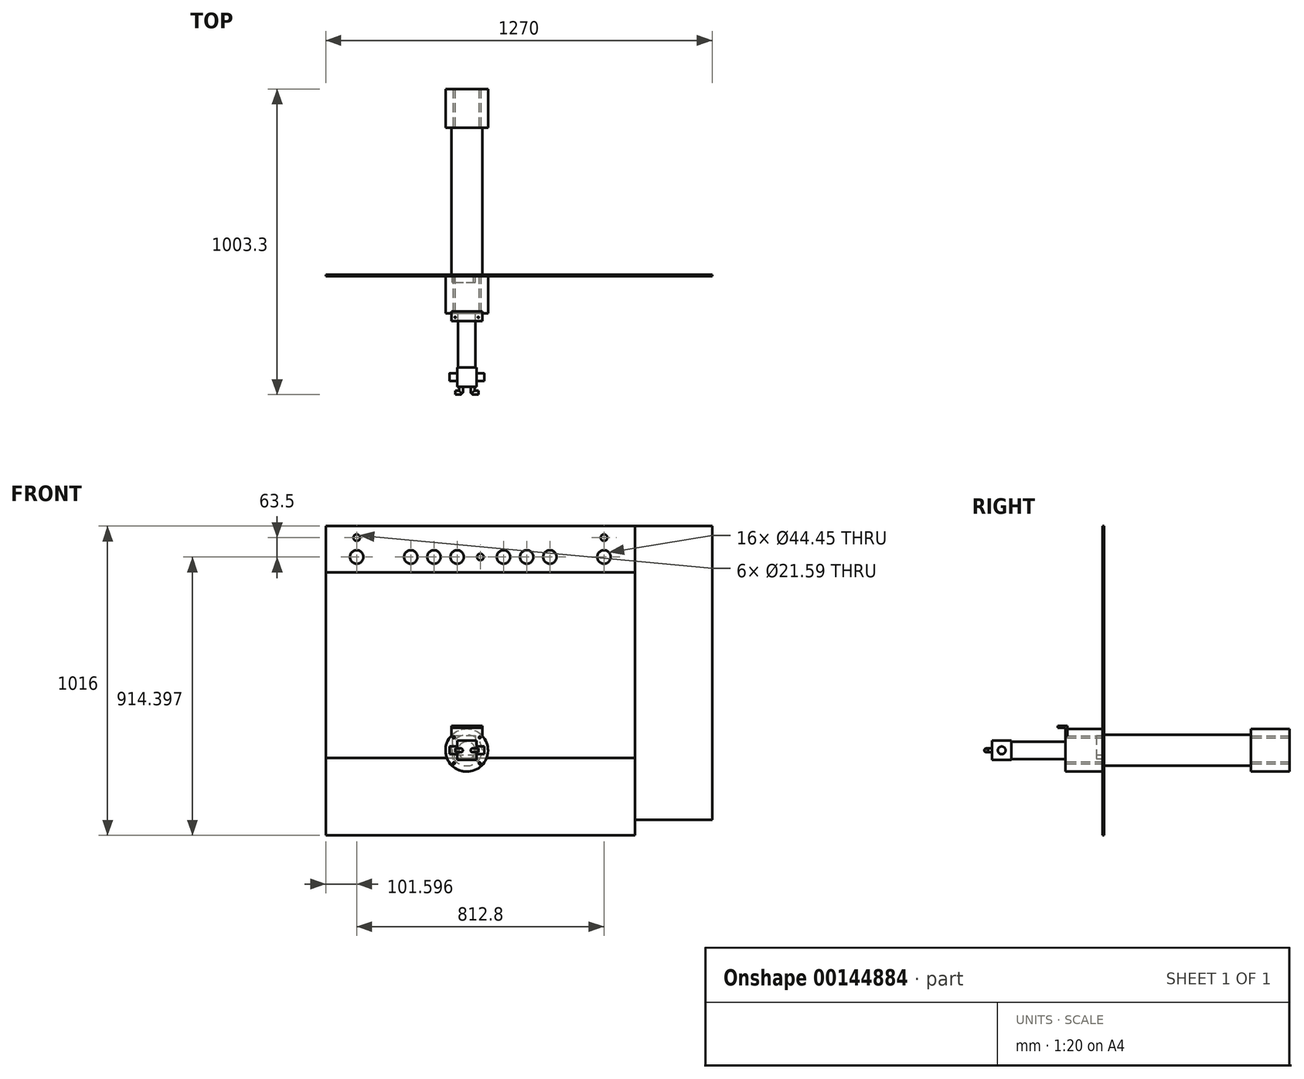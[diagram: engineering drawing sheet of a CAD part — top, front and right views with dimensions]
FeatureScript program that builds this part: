
annotation { "Feature Type Name" : "Feature", "Feature Type Description" : "" }
export const myFeature = defineFeature(function(context is Context, id is Id, definition is map)
    precondition{}
    {
        {
            var Q0;
            Q0=qCreatedBy(makeId("Front.planeOp"),FACE);
            var sketch = newSketch(context, id + "F0", { "sketchPlane" : qUnion([Q0])});
            skLineSegment(sketch, "E0.bottom", {"start": v(-463.31, 736.89) * mm, "end": v(552.69, 736.89) * mm});
            skLineSegment(sketch, "E0.top", {"start": v(-463.31, 584.49) * mm, "end": v(552.69, 584.49) * mm});
            skLineSegment(sketch, "E0.left", {"start": v(-463.31, 736.89) * mm, "end": v(-463.31, 584.49) * mm});
            skLineSegment(sketch, "E0.right", {"start": v(552.69, 736.89) * mm, "end": v(552.69, 584.49) * mm});
            skLineSegment(sketch, "E1.top", {"start": v(-463.31, -25.11) * mm, "end": v(552.69, -25.11) * mm});
            skLineSegment(sketch, "E1.left", {"start": v(-463.31, 584.49) * mm, "end": v(-463.31, -25.11) * mm});
            skLineSegment(sketch, "E1.right", {"start": v(552.69, 584.49) * mm, "end": v(552.69, -25.11) * mm});
            skLineSegment(sketch, "E2.top", {"start": v(-463.31, -279.11) * mm, "end": v(552.69, -279.11) * mm});
            skLineSegment(sketch, "E2.left", {"start": v(-463.31, -25.11) * mm, "end": v(-463.31, -279.11) * mm});
            skLineSegment(sketch, "E2.right", {"start": v(552.69, -25.11) * mm, "end": v(552.69, -279.11) * mm});
            skLineSegment(sketch, "E3.bottom", {"start": v(552.69, 736.89) * mm, "end": v(806.69, 736.89) * mm});
            skLineSegment(sketch, "E3.top", {"start": v(552.69, -228.31) * mm, "end": v(806.69, -228.31) * mm});
            skLineSegment(sketch, "E3.left", {"start": v(552.69, 736.89) * mm, "end": v(552.69, -228.31) * mm});
            skLineSegment(sketch, "E3.right", {"start": v(806.69, 736.89) * mm, "end": v(806.69, -228.31) * mm});
            skSolve(sketch);
        }
        {
            var Q0;
            Q0=makeQuery(id+"F0.imprint","IMPRINT",FACE,{"disambiguationData":[TD([[makeQuery(id+"F0.imprint","IMPRINT",EDGE,{"derivedFrom":sQuery(id+"F0.wireOp",EDGE,"E0.bottom")}),-1.0]])]});
            extrude(context, id + "F1", {"entities" : qUnion([Q0]), "depth" : 5.08 * mm});
        }
        {
            var Q0;
            Q0=makeQuery(id+"F0.imprint","IMPRINT",FACE,{"disambiguationData":[TD([[makeQuery(id+"F0.imprint","IMPRINT",EDGE,{"derivedFrom":sQuery(id+"F0.wireOp",EDGE,"E0.top")}),-1.0]])]});
            extrude(context, id + "F2", {"entities" : qUnion([Q0]), "depth" : 5.08 * mm});
        }
        {
            var Q0;
            Q0=makeQuery(id+"F0.imprint","IMPRINT",FACE,{"disambiguationData":[TD([[makeQuery(id+"F0.imprint","IMPRINT",EDGE,{"derivedFrom":sQuery(id+"F0.wireOp",EDGE,"E1.top")}),-1.0]])]});
            extrude(context, id + "F3", {"entities" : qUnion([Q0]), "depth" : 5.08 * mm});
        }
        {
            var Q0;
            {var subQ3=sQuery(id+"F0.wireOp",EDGE,"E3.bottom");Q0=makeQuery(id+"F0.imprint","IMPRINT",FACE,{"disambiguationData":[TD([[makeQuery(id+"F0.imprint","IMPRINT",EDGE,{"derivedFrom":subQ3}),-1.0]])]});}
            extrude(context, id + "F4", {"entities" : qUnion([Q0]), "depth" : 5.08 * mm});
        }
        {
            var Q0;
            Q0=qCreatedBy(makeId("Front.planeOp"),FACE);
            var sketch = newSketch(context, id + "F5", { "sketchPlane" : qUnion([Q0])});
            skCircle(sketch, "E4", {"center": v(0, 0) * mm, "radius": 69.85 * mm});
            skCircle(sketch, "E5", {"center": v(0, 0) * mm, "radius": 50.8 * mm});
            skCircle(sketch, "E6", {"center": v(0, 0) * mm, "radius": 28.58 * mm});
            skSolve(sketch);
        }
        {
            var Q0;
            Q0=makeQuery(id+"F5.imprint","IMPRINT",FACE,{"disambiguationData":[TD([[makeQuery(id+"F5.imprint","IMPRINT",EDGE,{"derivedFrom":sQuery(id+"F5.wireOp",EDGE,"E4")}),1.0]])]});
            var Q1;
            Q1=makeQuery(id+"F5.imprint","IMPRINT",FACE,{"disambiguationData":[TD([[makeQuery(id+"F5.imprint","IMPRINT",EDGE,{"derivedFrom":sQuery(id+"F5.wireOp",EDGE,"E5")}),1.0]])]});
            var Q2;
            Q2=makeQuery(id+"F5.imprint","IMPRINT",FACE,{"disambiguationData":[TD([[makeQuery(id+"F5.imprint","IMPRINT",EDGE,{"derivedFrom":sQuery(id+"F5.wireOp",EDGE,"E6")}),1.0]])]});
            extrude(context, id + "F6", {"entities" : qUnion([Q0, Q1, Q2]), "depth" : 127 * mm});
        }
        {
            var Q0;
            Q0=makeQuery(id+"F5.imprint","IMPRINT",FACE,{"disambiguationData":[TD([[makeQuery(id+"F5.imprint","IMPRINT",EDGE,{"derivedFrom":sQuery(id+"F5.wireOp",EDGE,"E5")}),1.0]])]});
            var Q1;
            Q1=makeQuery(id+"F5.imprint","IMPRINT",FACE,{"disambiguationData":[TD([[makeQuery(id+"F5.imprint","IMPRINT",EDGE,{"derivedFrom":sQuery(id+"F5.wireOp",EDGE,"E6")}),1.0]])]});
            extrude(context, id + "F7", {"entities" : qUnion([Q0, Q1]), "operationType" : NewBodyOperationType.ADD, "oppositeDirection" : true, "depth" : 482.6 * mm});
        }
        {
            var Q0;
            Q0=makeQuery(id+"F5.imprint","IMPRINT",FACE,{"disambiguationData":[TD([[makeQuery(id+"F5.imprint","IMPRINT",EDGE,{"derivedFrom":sQuery(id+"F5.wireOp",EDGE,"E4")}),1.0]])]});
            var Q1;
            Q1=makeQuery(id+"F5.imprint","IMPRINT",FACE,{"disambiguationData":[TD([[makeQuery(id+"F5.imprint","IMPRINT",EDGE,{"derivedFrom":sQuery(id+"F5.wireOp",EDGE,"E5")}),1.0]])]});
            var Q2;
            Q2=makeQuery(id+"F5.imprint","IMPRINT",FACE,{"disambiguationData":[TD([[makeQuery(id+"F5.imprint","IMPRINT",EDGE,{"derivedFrom":sQuery(id+"F5.wireOp",EDGE,"E6")}),1.0]])]});
            extrude(context, id + "F8", {"entities" : qUnion([Q0, Q1, Q2]), "operationType" : NewBodyOperationType.ADD, "oppositeDirection" : true, "depth" : 609.6 * mm, "hasSecondDirection" : true, "secondDirectionOppositeDirection" : true, "secondDirectionDepth" : 482.6 * mm});
        }
        {
            var Q0;
            Q0=makeQuery(id+"F5.imprint","IMPRINT",FACE,{"disambiguationData":[TD([[makeQuery(id+"F5.imprint","IMPRINT",EDGE,{"derivedFrom":sQuery(id+"F5.wireOp",EDGE,"E6")}),1.0]])]});
            extrude(context, id + "F9", {"entities" : qUnion([Q0]), "depth" : 304.8 * mm});
        }
        {
            var Q0;
            Q0=makeQuery(id+"F9.opExtrude","CAP_FACE",FACE,{"disambiguationData":[OSD([sQuery(id+"F5.wireOp",EDGE,"E6")])],"isStart":false});
            var sketch = newSketch(context, id + "F10", { "sketchPlane" : qUnion([Q0])});
            skLineSegment(sketch, "E7.bottom", {"start": v(-31.75, -31.75) * mm, "end": v(31.75, -31.75) * mm});
            skLineSegment(sketch, "E7.top", {"start": v(-31.75, 31.75) * mm, "end": v(31.75, 31.75) * mm});
            skLineSegment(sketch, "E7.left", {"start": v(-31.75, -31.75) * mm, "end": v(-31.75, 31.75) * mm});
            skLineSegment(sketch, "E7.right", {"start": v(31.75, -31.75) * mm, "end": v(31.75, 31.75) * mm});
            skSolve(sketch);
        }
        {
            var Q0;
            Q0=makeQuery(id+"F10.imprint","IMPRINT",FACE,{"disambiguationData":[TD([[makeQuery(id+"F10.imprint","IMPRINT",EDGE,{"derivedFrom":sQuery(id+"F10.wireOp",EDGE,"E7.bottom")}),1.0]])]});
            var Q1;
            Q1=makeQuery(id+"F10.imprint","IMPRINT",FACE,{"disambiguationData":[TD([[makeQuery(id+"F10.imprint","IMPRINT",EDGE,{"derivedFrom":makeQuery(id+"F9.opExtrude","CAP_EDGE",EDGE,{"disambiguationData":[OSD([sQuery(id+"F5.wireOp",EDGE,"E6")])],"isStart":false})}),1.0]])]});
            extrude(context, id + "F11", {"entities" : qUnion([Q0, Q1]), "operationType" : NewBodyOperationType.ADD, "depth" : 63.5 * mm});
        }
        {
            var Q0;
            Q0=makeQuery(id+"F11.opExtrude","SWEPT_FACE",FACE,{"disambiguationData":[OSD([sQuery(id+"F10.wireOp",EDGE,"E7.right")])]});
            var sketch = newSketch(context, id + "F12", { "sketchPlane" : qUnion([Q0])});
            skLineSegment(sketch, "E8", {"start": v(-336.55, -31.75) * mm, "end": v(-336.55, 31.75) * mm, "construction": true});
            skCircle(sketch, "E9", {"center": v(-336.55, 0) * mm, "radius": 12.7 * mm});
            skSolve(sketch);
        }
        {
            var Q0;
            Q0=makeQuery(id+"F12.imprint","IMPRINT",FACE,{"disambiguationData":[TD([[makeQuery(id+"F12.imprint","IMPRINT",EDGE,{"derivedFrom":sQuery(id+"F12.wireOp",EDGE,"E9")}),1.0]])]});
            extrude(context, id + "F13", {"entities" : qUnion([Q0]), "operationType" : NewBodyOperationType.ADD, "depth" : 25.4 * mm, "hasSecondDirection" : true, "secondDirectionOppositeDirection" : true, "secondDirectionDepth" : 88.9 * mm});
        }
        {
            var Q0;
            Q0=makeQuery(id+"F11.opExtrude","CAP_FACE",FACE,{"disambiguationData":[OSD([sQuery(id+"F10.wireOp",EDGE,"E7.bottom"),sQuery(id+"F10.wireOp",EDGE,"E7.top"),sQuery(id+"F10.wireOp",EDGE,"E7.left"),sQuery(id+"F10.wireOp",EDGE,"E7.right")])],"isStart":false});
            var sketch = newSketch(context, id + "F14", { "sketchPlane" : qUnion([Q0])});
            skLineSegment(sketch, "E10", {"start": v(-31.75, 0) * mm, "end": v(31.75, 0) * mm, "construction": true});
            skLineSegment(sketch, "E11.0", {"start": v(-19.05, -31.75) * mm, "end": v(-19.05, 31.75) * mm, "construction": true});
            skLineSegment(sketch, "E12.0", {"start": v(19.05, -31.75) * mm, "end": v(19.05, 31.75) * mm, "construction": true});
            skCircle(sketch, "E13", {"center": v(-19.05, 0) * mm, "radius": 6.35 * mm});
            skCircle(sketch, "E14", {"center": v(19.05, 0) * mm, "radius": 6.35 * mm});
            skSolve(sketch);
        }
        {
            var Q0;
            Q0=makeQuery(id+"F14.imprint","IMPRINT",FACE,{"disambiguationData":[TD([[makeQuery(id+"F14.imprint","IMPRINT",EDGE,{"derivedFrom":sQuery(id+"F14.wireOp",EDGE,"E13")}),1.0]])]});
            var Q1;
            Q1=makeQuery(id+"F14.imprint","IMPRINT",FACE,{"disambiguationData":[TD([[makeQuery(id+"F14.imprint","IMPRINT",EDGE,{"derivedFrom":sQuery(id+"F14.wireOp",EDGE,"E14")}),1.0]])]});
            extrude(context, id + "F15", {"entities" : qUnion([Q0, Q1]), "operationType" : NewBodyOperationType.ADD, "depth" : 19.05 * mm});
        }
        {
            var Q0;
            Q0=makeQuery(id+"F11.opExtrude","SWEPT_FACE",FACE,{"disambiguationData":[OSD([sQuery(id+"F10.wireOp",EDGE,"E7.left")])]});
            var sketch = newSketch(context, id + "F16", { "sketchPlane" : qUnion([Q0])});
            skLineSegment(sketch, "E15.0", {"start": v(387.35, -31.75) * mm, "end": v(387.35, 31.75) * mm, "construction": true});
            skCircle(sketch, "E16", {"center": v(387.35, 0) * mm, "radius": 6.35 * mm});
            skSolve(sketch);
        }
        {
            var Q0;
            Q0=makeQuery(id+"F16.imprint","IMPRINT",FACE,{"disambiguationData":[TD([[makeQuery(id+"F16.imprint","IMPRINT",EDGE,{"derivedFrom":sQuery(id+"F16.wireOp",EDGE,"E16")}),1.0]])]});
            extrude(context, id + "F17", {"entities" : qUnion([Q0]), "operationType" : NewBodyOperationType.ADD, "depth" : 6.35 * mm, "hasSecondDirection" : true, "secondDirectionOppositeDirection" : true, "secondDirectionDepth" : 12.7 * mm});
        }
        {
            var Q0;
            Q0=makeQuery(id+"F17.boolean.opBoolean","INTERSECT",EDGE,{"derivedFrom":[makeQuery(id+"F15.opExtrude","CAP_FACE",FACE,{"disambiguationData":[OSD([sQuery(id+"F14.wireOp",EDGE,"E13")])],"isStart":false}),makeQuery(id+"F17.opExtrude","CAP_FACE",FACE,{"disambiguationData":[OSD([sQuery(id+"F16.wireOp",EDGE,"E16")])],"isStart":true})]});
            chamfer(context, id + "F18", {"entities" : qUnion([Q0]), "width" : 6.35 * mm, "tangentPropagation" : true});
        }
        {
            var Q0;
            Q0=makeQuery(id+"F16.imprint","IMPRINT",FACE,{"disambiguationData":[TD([[makeQuery(id+"F16.imprint","IMPRINT",EDGE,{"derivedFrom":sQuery(id+"F16.wireOp",EDGE,"E16")}),1.0]])]});
            extrude(context, id + "F19", {"entities" : qUnion([Q0]), "operationType" : NewBodyOperationType.ADD, "oppositeDirection" : true, "depth" : 69.85 * mm, "hasSecondDirection" : true, "secondDirectionOppositeDirection" : true, "secondDirectionDepth" : 50.8 * mm});
        }
        {
            var Q0;
            Q0=makeQuery(id+"F19.boolean.opBoolean","INTERSECT",EDGE,{"derivedFrom":[makeQuery(id+"F15.opExtrude","CAP_FACE",FACE,{"disambiguationData":[OSD([sQuery(id+"F14.wireOp",EDGE,"E14")])],"isStart":false}),makeQuery(id+"F19.opExtrude","CAP_FACE",FACE,{"disambiguationData":[OSD([sQuery(id+"F16.wireOp",EDGE,"E16")])],"isStart":true})]});
            chamfer(context, id + "F20", {"entities" : qUnion([Q0]), "width" : 6.35 * mm, "tangentPropagation" : true});
        }
        {
            var Q0;
            Q0=makeQuery(id+"F6.opExtrude","CAP_FACE",FACE,{"disambiguationData":[OSD([sQuery(id+"F5.wireOp",EDGE,"E4")])],"isStart":false});
            var sketch = newSketch(context, id + "F21", { "sketchPlane" : qUnion([Q0])});
            skLineSegment(sketch, "E17.bottom", {"start": v(-42.5, 42.5) * mm, "end": v(42.5, 42.5) * mm, "construction": true});
            skLineSegment(sketch, "E17.top", {"start": v(-42.5, -42.5) * mm, "end": v(42.5, -42.5) * mm, "construction": true});
            skLineSegment(sketch, "E17.left", {"start": v(-42.5, 42.5) * mm, "end": v(-42.5, -42.5) * mm, "construction": true});
            skLineSegment(sketch, "E17.right", {"start": v(42.5, 42.5) * mm, "end": v(42.5, -42.5) * mm, "construction": true});
            skLineSegment(sketch, "E18", {"start": v(-69.85, 0) * mm, "end": v(69.85, 0) * mm, "construction": true});
            skLineSegment(sketch, "E19", {"start": v(0, 69.85) * mm, "end": v(0, -69.85) * mm, "construction": true});
            skPoint(sketch, "E19.startSnap0", {"position": v(0, 0) * mm});
            skCircle(sketch, "E20", {"center": v(-42.5, 42.5) * mm, "radius": 3.17 * mm});
            skCircle(sketch, "E21", {"center": v(42.5, 42.5) * mm, "radius": 3.17 * mm});
            skCircle(sketch, "E22", {"center": v(42.5, -42.5) * mm, "radius": 3.17 * mm});
            skCircle(sketch, "E23", {"center": v(-42.5, -42.5) * mm, "radius": 3.17 * mm});
            skCircle(sketch, "E24.cCircle", {"center": v(0, 0) * mm, "radius": 20 * mm, "construction": true});
            skLineSegment(sketch, "E24.0", {"start": v(7.45, 21.86) * mm, "end": v(22.66, 4.48) * mm});
            skLineSegment(sketch, "E24.1", {"start": v(22.66, 4.48) * mm, "end": v(15.2, -17.38) * mm});
            skLineSegment(sketch, "E24.2", {"start": v(15.2, -17.38) * mm, "end": v(-7.45, -21.86) * mm});
            skLineSegment(sketch, "E24.3", {"start": v(-7.45, -21.86) * mm, "end": v(-22.66, -4.48) * mm});
            skLineSegment(sketch, "E24.4", {"start": v(-22.66, -4.48) * mm, "end": v(-15.2, 17.38) * mm});
            skLineSegment(sketch, "E24.5", {"start": v(-15.2, 17.38) * mm, "end": v(7.45, 21.86) * mm});
            skPoint(sketch, "E24.0.midPoint", {"position": v(15.05, 13.17) * mm});
            skSolve(sketch);
        }
        {
            var Q0;
            Q0=makeQuery(id+"F21.imprint","IMPRINT",FACE,{"disambiguationData":[TD([[makeQuery(id+"F21.imprint","IMPRINT",EDGE,{"derivedFrom":sQuery(id+"F21.wireOp",EDGE,"E24.0")}),-1.0]])]});
            extrude(context, id + "F22", {"entities" : qUnion([Q0]), "operationType" : NewBodyOperationType.ADD, "depth" : 40 * mm});
        }
        {
            var Q0;
            Q0=makeQuery(id+"F21.imprint","IMPRINT",FACE,{"disambiguationData":[TD([[makeQuery(id+"F21.imprint","IMPRINT",EDGE,{"derivedFrom":sQuery(id+"F21.wireOp",EDGE,"E20")}),1.0]])]});
            var Q1;
            Q1=makeQuery(id+"F21.imprint","IMPRINT",FACE,{"disambiguationData":[TD([[makeQuery(id+"F21.imprint","IMPRINT",EDGE,{"derivedFrom":sQuery(id+"F21.wireOp",EDGE,"E21")}),1.0]])]});
            var Q2;
            Q2=makeQuery(id+"F21.imprint","IMPRINT",FACE,{"disambiguationData":[TD([[makeQuery(id+"F21.imprint","IMPRINT",EDGE,{"derivedFrom":sQuery(id+"F21.wireOp",EDGE,"E22")}),1.0]])]});
            var Q3;
            Q3=makeQuery(id+"F21.imprint","IMPRINT",FACE,{"disambiguationData":[TD([[makeQuery(id+"F21.imprint","IMPRINT",EDGE,{"derivedFrom":sQuery(id+"F21.wireOp",EDGE,"E23")}),1.0]])]});
            extrude(context, id + "F23", {"entities" : qUnion([Q0, Q1, Q2, Q3]), "operationType" : NewBodyOperationType.REMOVE, "oppositeDirection" : true, "depth" : 762 * mm});
        }
        {
            var Q0;
            Q0=makeQuery(id+"F21.imprint","IMPRINT",FACE,{"disambiguationData":[TD([[makeQuery(id+"F21.imprint","IMPRINT",EDGE,{"derivedFrom":sQuery(id+"F21.wireOp",EDGE,"E20")}),-1.0]])]});
            var sketch = newSketch(context, id + "F24", { "sketchPlane" : qUnion([Q0])});
            skCircle(sketch, "E25.0", {"center": v(-42.5, 42.5) * mm, "radius": 3.17 * mm});
            skCircle(sketch, "E25.1", {"center": v(42.5, 42.5) * mm, "radius": 3.17 * mm});
            skCircle(sketch, "E25.2", {"center": v(42.5, -42.5) * mm, "radius": 3.17 * mm});
            skCircle(sketch, "E25.3", {"center": v(-42.5, -42.5) * mm, "radius": 3.17 * mm});
            skLineSegment(sketch, "E25.4", {"start": v(-42.5, 42.5) * mm, "end": v(42.5, 42.5) * mm});
            skLineSegment(sketch, "E26", {"start": v(-42.5, 87.67) * mm, "end": v(-42.5, -59.76) * mm, "construction": true});
            skLineSegment(sketch, "E27", {"start": v(-42.5, -59.76) * mm, "end": v(42.5, -59.76) * mm, "construction": true});
            skLineSegment(sketch, "E28", {"start": v(42.5, -59.76) * mm, "end": v(42.5, 94.76) * mm, "construction": true});
            skCircle(sketch, "E29.0", {"center": v(0, 0) * mm, "radius": 79.85 * mm, "construction": true});
            skLineSegment(sketch, "E30", {"start": v(0, 70.78) * mm, "end": v(0, 79.85) * mm, "construction": true});
            skLineSegment(sketch, "E31", {"start": v(-42.5, 79.85) * mm, "end": v(42.5, 79.85) * mm, "construction": true});
            skLineSegment(sketch, "E32.0", {"start": v(50.8, -59.76) * mm, "end": v(50.8, 94.76) * mm});
            skLineSegment(sketch, "E33.0", {"start": v(36.14, -59.76) * mm, "end": v(36.14, 29.05) * mm});
            skLineSegment(sketch, "E34.0", {"start": v(-50.81, 87.67) * mm, "end": v(-50.81, -59.76) * mm});
            skLineSegment(sketch, "E35.0", {"start": v(-36.16, 87.67) * mm, "end": v(-36.16, 79.85) * mm});
            skLineSegment(sketch, "E36", {"start": v(-50.81, 79.85) * mm, "end": v(50.8, 79.85) * mm});
            skLineSegment(sketch, "E37.0", {"start": v(-50.81, 73.5) * mm, "end": v(50.8, 73.5) * mm});
            skLineSegment(sketch, "E38.0", {"start": v(-50.81, 29.05) * mm, "end": v(50.8, 29.05) * mm});
            skLineSegment(sketch, "E39.trimOffspring", {"start": v(-36.16, 29.05) * mm, "end": v(-36.16, -59.76) * mm});
            skLineSegment(sketch, "E40.trimOffspring", {"start": v(36.14, 42.5) * mm, "end": v(36.14, 73.5) * mm});
            skLineSegment(sketch, "E41.trimOffspring", {"start": v(-36.16, 73.5) * mm, "end": v(-36.16, 42.5) * mm});
            skLineSegment(sketch, "E42.trimOffspring", {"start": v(36.14, 79.85) * mm, "end": v(36.14, 94.76) * mm});
            skSolve(sketch);
        }
        {
            var Q0;
            {var subQ0=sQuery(id+"F24.wireOp",EDGE,"E36");var subQ1=sQuery(id+"F24.wireOp",EDGE,"E33.0");var subQ2=makeQuery(id+"F24.imprint","INTERSECT",VERTEX,{"derivedFrom":[subQ1,subQ0]});Q0=makeQuery(id+"F24.imprint","IMPRINT",FACE,{"disambiguationData":[TD([[makeQuery(id+"F24.imprint","IMPRINT",EDGE,{"disambiguationData":[TD([[subQ2,1.0]])],"derivedFrom":subQ1}),1.0]])]});}
            var Q1;
            {var subQ0=sQuery(id+"F24.wireOp",EDGE,"E36");var subQ1=sQuery(id+"F24.wireOp",EDGE,"E34.0");var subQ2=makeQuery(id+"F24.imprint","INTERSECT",VERTEX,{"derivedFrom":[subQ1,subQ0]});Q1=makeQuery(id+"F24.imprint","IMPRINT",FACE,{"disambiguationData":[TD([[makeQuery(id+"F24.imprint","IMPRINT",EDGE,{"disambiguationData":[TD([[subQ2,-1.0]])],"derivedFrom":subQ1}),1.0]])]});}
            var Q2;
            {var subQ0=sQuery(id+"F24.wireOp",EDGE,"E36");var subQ1=sQuery(id+"F24.wireOp",EDGE,"E32.0");var subQ2=makeQuery(id+"F24.imprint","INTERSECT",VERTEX,{"derivedFrom":[subQ1,subQ0]});Q2=makeQuery(id+"F24.imprint","IMPRINT",FACE,{"disambiguationData":[TD([[makeQuery(id+"F24.imprint","IMPRINT",EDGE,{"disambiguationData":[TD([[subQ2,1.0]])],"derivedFrom":subQ1}),1.0]])]});}
            extrude(context, id + "F25", {"entities" : qUnion([Q0, Q1, Q2]), "depth" : 25.4 * mm, "hasSecondDirection" : true, "secondDirectionOppositeDirection" : true, "secondDirectionDepth" : 6.35 * mm});
        }
        {
            var Q0;
            {var subQ0=sQuery(id+"F24.wireOp",EDGE,"E37.0");var subQ1=sQuery(id+"F24.wireOp",EDGE,"E34.0");var subQ2=makeQuery(id+"F24.imprint","INTERSECT",VERTEX,{"derivedFrom":[subQ1,subQ0]});Q0=makeQuery(id+"F24.imprint","IMPRINT",FACE,{"disambiguationData":[TD([[makeQuery(id+"F24.imprint","IMPRINT",EDGE,{"disambiguationData":[TD([[subQ2,-1.0]])],"derivedFrom":subQ1}),1.0]])]});}
            var Q1;
            Q1=makeQuery(id+"F24.imprint","IMPRINT",FACE,{"disambiguationData":[TD([[makeQuery(id+"F24.imprint","IMPRINT",EDGE,{"derivedFrom":sQuery(id+"F24.wireOp",EDGE,"E25.0")}),-1.0]])]});
            var Q2;
            {var subQ0=sQuery(id+"F24.wireOp",EDGE,"E37.0");var subQ1=sQuery(id+"F24.wireOp",EDGE,"E32.0");var subQ2=makeQuery(id+"F24.imprint","INTERSECT",VERTEX,{"derivedFrom":[subQ1,subQ0]});Q2=makeQuery(id+"F24.imprint","IMPRINT",FACE,{"disambiguationData":[TD([[makeQuery(id+"F24.imprint","IMPRINT",EDGE,{"disambiguationData":[TD([[subQ2,1.0]])],"derivedFrom":subQ1}),1.0]])]});}
            var Q3;
            {var subQ0=sQuery(id+"F24.wireOp",EDGE,"E40.trimOffspring");var subQ1=sQuery(id+"F24.wireOp",EDGE,"E37.0");var subQ2=makeQuery(id+"F24.imprint","INTERSECT",VERTEX,{"derivedFrom":[subQ1,subQ0]});Q3=makeQuery(id+"F24.imprint","IMPRINT",FACE,{"disambiguationData":[TD([[makeQuery(id+"F24.imprint","IMPRINT",EDGE,{"disambiguationData":[TD([[subQ2,1.0]])],"derivedFrom":subQ1}),-1.0]])]});}
            var Q4;
            {var subQ0=sQuery(id+"F24.wireOp",EDGE,"E40.trimOffspring");var subQ1=sQuery(id+"F24.wireOp",EDGE,"E25.4");var subQ2=makeQuery(id+"F24.imprint","INTERSECT",VERTEX,{"derivedFrom":[subQ1,subQ0]});Q4=makeQuery(id+"F24.imprint","IMPRINT",FACE,{"disambiguationData":[TD([[makeQuery(id+"F24.imprint","IMPRINT",EDGE,{"disambiguationData":[TD([[subQ2,1.0]])],"derivedFrom":subQ1}),1.0]])]});}
            extrude(context, id + "F26", {"entities" : qUnion([Q0, Q1, Q2, Q3, Q4]), "operationType" : NewBodyOperationType.ADD, "oppositeDirection" : true, "depth" : 6.35 * mm});
        }
        {
            var Q0;
            Q0=makeQuery(id+"F25.opExtrude","SWEPT_FACE",FACE,{"disambiguationData":[OSD([sQuery(id+"F24.wireOp",EDGE,"E36")])]});
            var sketch = newSketch(context, id + "F27", { "sketchPlane" : qUnion([Q0])});
            skLineSegment(sketch, "E43.0", {"start": v(-48.86, -139.9) * mm, "end": v(48.84, -139.9) * mm, "construction": true});
            skLineSegment(sketch, "E44.0", {"start": v(-38.11, -152.4) * mm, "end": v(-38.11, -127.4) * mm, "construction": true});
            skLineSegment(sketch, "E45.0", {"start": v(38.1, -152.4) * mm, "end": v(38.1, -120.65) * mm, "construction": true});
            skCircle(sketch, "E46", {"center": v(38.1, -139.9) * mm, "radius": 2 * mm});
            skCircle(sketch, "E47", {"center": v(-38.11, -139.9) * mm, "radius": 2 * mm});
            skSolve(sketch);
        }
        {
            var Q0;
            Q0=makeQuery(id+"F27.imprint","IMPRINT",FACE,{"disambiguationData":[TD([[makeQuery(id+"F27.imprint","IMPRINT",EDGE,{"derivedFrom":sQuery(id+"F27.wireOp",EDGE,"E46")}),1.0]])]});
            var Q1;
            Q1=makeQuery(id+"F27.imprint","IMPRINT",FACE,{"disambiguationData":[TD([[makeQuery(id+"F27.imprint","IMPRINT",EDGE,{"derivedFrom":sQuery(id+"F27.wireOp",EDGE,"E47")}),1.0]])]});
            extrude(context, id + "F28", {"entities" : qUnion([Q0, Q1]), "operationType" : NewBodyOperationType.REMOVE, "oppositeDirection" : true, "depth" : 25.4 * mm});
        }
        {
            var Q0;
            Q0=qCreatedBy(makeId("Front.planeOp"),FACE);
            var sketch = newSketch(context, id + "F29", { "sketchPlane" : qUnion([Q0])});
            skLineSegment(sketch, "E48.bottom", {"start": v(-47.82, 48.82) * mm, "end": v(28.38, 48.82) * mm});
            skLineSegment(sketch, "E48.top", {"start": v(-47.82, -27.38) * mm, "end": v(28.38, -27.38) * mm});
            skLineSegment(sketch, "E48.left", {"start": v(-47.82, 48.82) * mm, "end": v(-47.82, -27.38) * mm});
            skLineSegment(sketch, "E48.right", {"start": v(28.38, 48.82) * mm, "end": v(28.38, -27.38) * mm});
            skLineSegment(sketch, "E49.0", {"start": v(-41.47, -14.68) * mm, "end": v(-41.47, -27.38) * mm});
            skLineSegment(sketch, "E50.0", {"start": v(22.03, -14.68) * mm, "end": v(22.03, -27.38) * mm});
            skLineSegment(sketch, "E51.0", {"start": v(-41.47, -14.68) * mm, "end": v(22.03, -14.68) * mm});
            skSolve(sketch);
        }
        {
            var Q0;
            Q0=makeQuery(id+"F29.imprint","IMPRINT",FACE,{"disambiguationData":[TD([[makeQuery(id+"F29.imprint","IMPRINT",EDGE,{"derivedFrom":sQuery(id+"F29.wireOp",EDGE,"E48.bottom")}),-1.0]])]});
            extrude(context, id + "F30", {"entities" : qUnion([Q0]), "depth" : 25.4 * mm});
        }
        {
            var Q0;
            Q0=makeQuery(id+"F1.opExtrude","SWEPT_BODY",BODY,{"disambiguationData":[OSD([sQuery(id+"F0.wireOp",EDGE,"E0.bottom"),sQuery(id+"F0.wireOp",EDGE,"E0.left"),sQuery(id+"F0.wireOp",EDGE,"E0.top"),sQuery(id+"F0.wireOp",EDGE,"E3.left")])]});
            transform(context, id + "F31", {"entities" : qUnion([Q0]), "transformType" : TransformType.TRANSLATION_3D, "dx" : 0 * mm, "dy" : 0 * mm, "dz" : 0 * mm, "makeCopy" : true});
        }
        {
            var Q0;
            Q0=makeQuery(id+"F31.opPattern","COPY",FACE,{"derivedFrom":makeQuery(id+"F1.opExtrude","CAP_FACE",FACE,{"disambiguationData":[OSD([sQuery(id+"F0.wireOp",EDGE,"E0.bottom"),sQuery(id+"F0.wireOp",EDGE,"E0.left"),sQuery(id+"F0.wireOp",EDGE,"E0.top"),sQuery(id+"F0.wireOp",EDGE,"E3.left")])],"isStart":false}),"instanceName":"1"});
            var sketch = newSketch(context, id + "F32", { "sketchPlane" : qUnion([Q0])});
            skLineSegment(sketch, "E52.0", {"start": v(-361.71, 736.89) * mm, "end": v(-361.71, 584.49) * mm, "construction": true});
            skLineSegment(sketch, "E53.0", {"start": v(451.09, 736.89) * mm, "end": v(451.09, 584.49) * mm, "construction": true});
            skLineSegment(sketch, "E54.0", {"start": v(-463.31, 635.29) * mm, "end": v(552.69, 635.29) * mm, "construction": true});
            skLineSegment(sketch, "E55.0", {"start": v(-463.31, 698.79) * mm, "end": v(552.69, 698.79) * mm, "construction": true});
            skLineSegment(sketch, "E56", {"start": v(44.69, 736.89) * mm, "end": v(44.69, 584.49) * mm, "construction": true});
            skLineSegment(sketch, "E57.0", {"start": v(-31.51, 736.89) * mm, "end": v(-31.51, 584.49) * mm, "construction": true});
            skLineSegment(sketch, "E58.0", {"start": v(120.89, 736.89) * mm, "end": v(120.89, 584.49) * mm, "construction": true});
            skLineSegment(sketch, "E59.0", {"start": v(197.09, 736.89) * mm, "end": v(197.09, 584.49) * mm, "construction": true});
            skLineSegment(sketch, "E60.0", {"start": v(-107.71, 736.89) * mm, "end": v(-107.71, 584.49) * mm, "construction": true});
            skLineSegment(sketch, "E61.0", {"start": v(273.29, 736.89) * mm, "end": v(273.29, 584.49) * mm, "construction": true});
            skLineSegment(sketch, "E62.0", {"start": v(-183.91, 736.89) * mm, "end": v(-183.91, 584.49) * mm, "construction": true});
            skCircle(sketch, "E63", {"center": v(-361.71, 635.29) * mm, "radius": 22.23 * mm});
            skCircle(sketch, "E64", {"center": v(-183.91, 635.29) * mm, "radius": 22.23 * mm});
            skCircle(sketch, "E65", {"center": v(-107.71, 635.29) * mm, "radius": 22.23 * mm});
            skCircle(sketch, "E66", {"center": v(-31.51, 635.29) * mm, "radius": 22.23 * mm});
            skCircle(sketch, "E67", {"center": v(120.89, 635.29) * mm, "radius": 22.23 * mm});
            skCircle(sketch, "E68", {"center": v(197.09, 635.29) * mm, "radius": 22.23 * mm});
            skCircle(sketch, "E69", {"center": v(273.29, 635.29) * mm, "radius": 22.23 * mm});
            skCircle(sketch, "E70", {"center": v(451.09, 635.29) * mm, "radius": 22.23 * mm});
            skCircle(sketch, "E71", {"center": v(451.09, 698.79) * mm, "radius": 10.8 * mm});
            skCircle(sketch, "E72", {"center": v(-361.71, 698.79) * mm, "radius": 10.8 * mm});
            skCircle(sketch, "E73", {"center": v(44.69, 635.29) * mm, "radius": 10.8 * mm});
            skSolve(sketch);
        }
        {
            var Q0;
            Q0=makeQuery(id+"F32.imprint","IMPRINT",FACE,{"disambiguationData":[TD([[makeQuery(id+"F32.imprint","IMPRINT",EDGE,{"derivedFrom":sQuery(id+"F32.wireOp",EDGE,"E72")}),1.0]])]});
            var Q1;
            Q1=makeQuery(id+"F32.imprint","IMPRINT",FACE,{"disambiguationData":[TD([[makeQuery(id+"F32.imprint","IMPRINT",EDGE,{"derivedFrom":sQuery(id+"F32.wireOp",EDGE,"E63")}),1.0]])]});
            var Q2;
            Q2=makeQuery(id+"F32.imprint","IMPRINT",FACE,{"disambiguationData":[TD([[makeQuery(id+"F32.imprint","IMPRINT",EDGE,{"derivedFrom":sQuery(id+"F32.wireOp",EDGE,"E64")}),1.0]])]});
            var Q3;
            Q3=makeQuery(id+"F32.imprint","IMPRINT",FACE,{"disambiguationData":[TD([[makeQuery(id+"F32.imprint","IMPRINT",EDGE,{"derivedFrom":sQuery(id+"F32.wireOp",EDGE,"E65")}),1.0]])]});
            var Q4;
            Q4=makeQuery(id+"F32.imprint","IMPRINT",FACE,{"disambiguationData":[TD([[makeQuery(id+"F32.imprint","IMPRINT",EDGE,{"derivedFrom":sQuery(id+"F32.wireOp",EDGE,"E66")}),1.0]])]});
            var Q5;
            Q5=makeQuery(id+"F32.imprint","IMPRINT",FACE,{"disambiguationData":[TD([[makeQuery(id+"F32.imprint","IMPRINT",EDGE,{"derivedFrom":sQuery(id+"F32.wireOp",EDGE,"E73")}),1.0]])]});
            var Q6;
            Q6=makeQuery(id+"F32.imprint","IMPRINT",FACE,{"disambiguationData":[TD([[makeQuery(id+"F32.imprint","IMPRINT",EDGE,{"derivedFrom":sQuery(id+"F32.wireOp",EDGE,"E67")}),1.0]])]});
            var Q7;
            Q7=makeQuery(id+"F32.imprint","IMPRINT",FACE,{"disambiguationData":[TD([[makeQuery(id+"F32.imprint","IMPRINT",EDGE,{"derivedFrom":sQuery(id+"F32.wireOp",EDGE,"E69")}),1.0]])]});
            var Q8;
            Q8=makeQuery(id+"F32.imprint","IMPRINT",FACE,{"disambiguationData":[TD([[makeQuery(id+"F32.imprint","IMPRINT",EDGE,{"derivedFrom":sQuery(id+"F32.wireOp",EDGE,"E68")}),1.0]])]});
            var Q9;
            Q9=makeQuery(id+"F32.imprint","IMPRINT",FACE,{"disambiguationData":[TD([[makeQuery(id+"F32.imprint","IMPRINT",EDGE,{"derivedFrom":sQuery(id+"F32.wireOp",EDGE,"E70")}),1.0]])]});
            var Q10;
            Q10=makeQuery(id+"F32.imprint","IMPRINT",FACE,{"disambiguationData":[TD([[makeQuery(id+"F32.imprint","IMPRINT",EDGE,{"derivedFrom":sQuery(id+"F32.wireOp",EDGE,"E71")}),1.0]])]});
            extrude(context, id + "F33", {"entities" : qUnion([Q0, Q1, Q2, Q3, Q4, Q5, Q6, Q7, Q8, Q9, Q10]), "operationType" : NewBodyOperationType.REMOVE, "oppositeDirection" : true, "depth" : 25.4 * mm});
        }
        {
            var Q0;
            {var subQ0=sQuery(id+"F0.wireOp",EDGE,"E0.bottom");Q0=makeQuery(id+"F0.imprint","IMPRINT",FACE,{"disambiguationData":[TD([[makeQuery(id+"F0.imprint","IMPRINT",EDGE,{"derivedFrom":subQ0}),-1.0]])]});}
            var Q1;
            {var subQ0=sQuery(id+"F0.wireOp",EDGE,"E0.top");Q1=makeQuery(id+"F0.imprint","IMPRINT",FACE,{"disambiguationData":[TD([[makeQuery(id+"F0.imprint","IMPRINT",EDGE,{"derivedFrom":subQ0}),-1.0]])]});}
            extrude(context, id + "F34", {"entities" : qUnion([Q0, Q1]), "depth" : 5.08 * mm});
        }
    });
